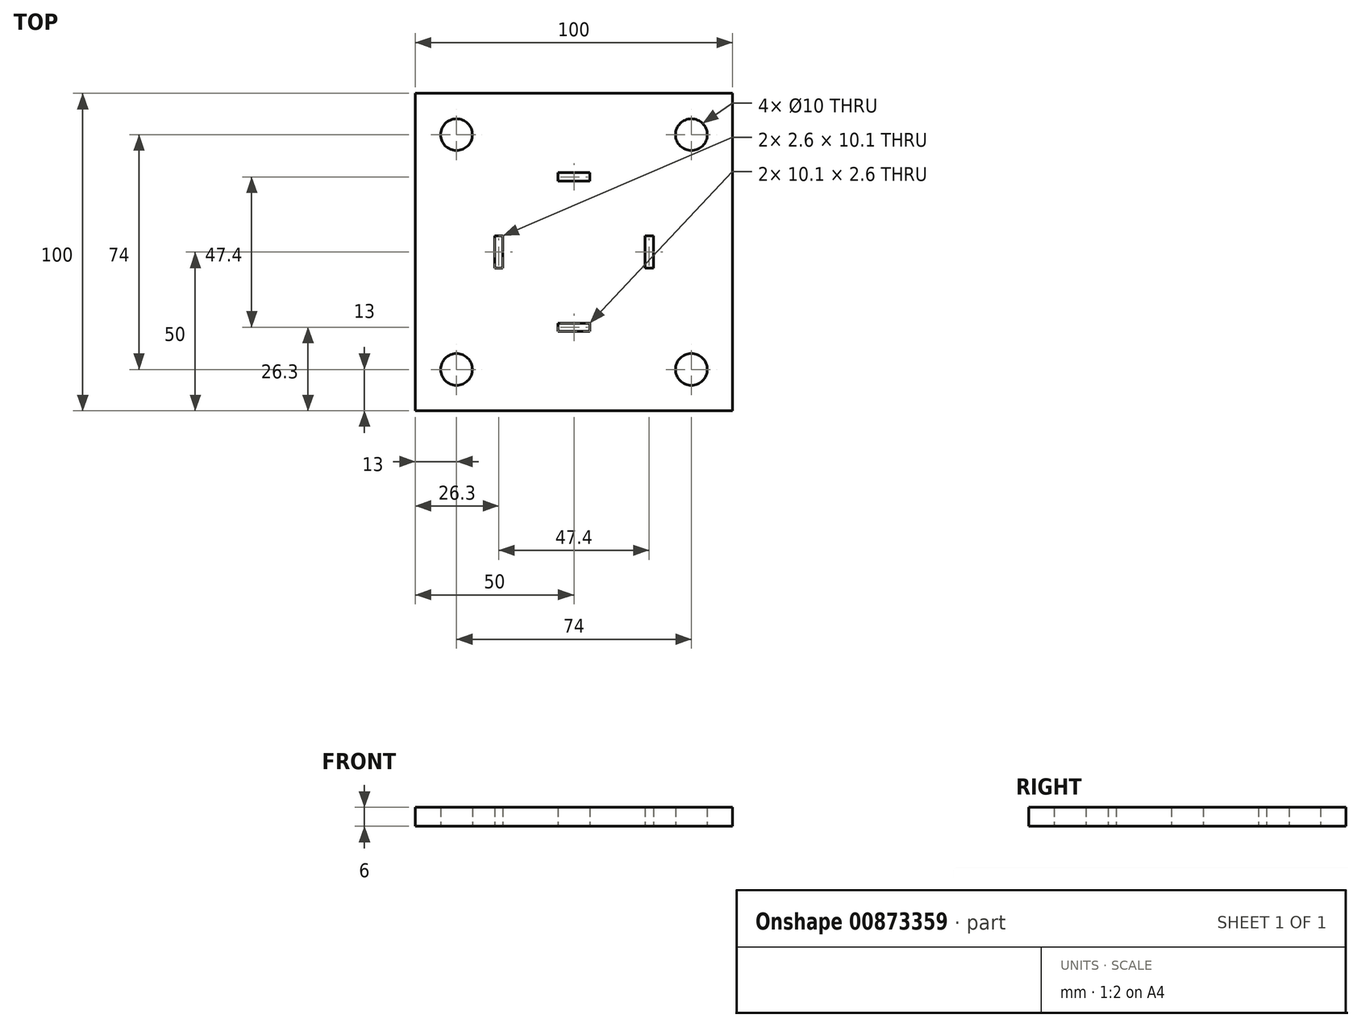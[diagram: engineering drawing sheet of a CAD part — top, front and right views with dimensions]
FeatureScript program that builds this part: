
annotation { "Feature Type Name" : "Feature", "Feature Type Description" : "" }
export const myFeature = defineFeature(function(context is Context, id is Id, definition is map)
    precondition{}
    {
        {
            var Q0;
            Q0=qCreatedBy(makeId("Top.planeOp"),FACE);
            var sketch = newSketch(context, id + "F0", { "sketchPlane" : qUnion([Q0])});
            skLineSegment(sketch, "E0.bottom", {"start": v(-50, 50) * mm, "end": v(50, 50) * mm});
            skLineSegment(sketch, "E0.top", {"start": v(-50, -50) * mm, "end": v(50, -50) * mm});
            skLineSegment(sketch, "E0.left", {"start": v(-50, 50) * mm, "end": v(-50, -50) * mm});
            skLineSegment(sketch, "E0.right", {"start": v(50, 50) * mm, "end": v(50, -50) * mm});
            skPoint(sketch, "E0.middle", {"position": v(0, 0) * mm});
            skLineSegment(sketch, "E1", {"start": v(-50, 50) * mm, "end": v(50, -50) * mm, "construction": true});
            skLineSegment(sketch, "E2", {"start": v(50, 50) * mm, "end": v(-50, -50) * mm, "construction": true});
            skLineSegment(sketch, "E3.bottom", {"start": v(25, 25) * mm, "end": v(-25, 25) * mm, "construction": true});
            skLineSegment(sketch, "E3.top", {"start": v(25, -25) * mm, "end": v(-25, -25) * mm, "construction": true});
            skLineSegment(sketch, "E3.left", {"start": v(25, 25) * mm, "end": v(25, -25) * mm, "construction": true});
            skLineSegment(sketch, "E3.right", {"start": v(-25, 25) * mm, "end": v(-25, -25) * mm, "construction": true});
            skLineSegment(sketch, "E4.bottom", {"start": v(-5.05, 25) * mm, "end": v(5.05, 25) * mm});
            skLineSegment(sketch, "E4.top", {"start": v(-5.05, 22.4) * mm, "end": v(5.05, 22.4) * mm});
            skLineSegment(sketch, "E4.left", {"start": v(-5.05, 25) * mm, "end": v(-5.05, 22.4) * mm});
            skLineSegment(sketch, "E4.right", {"start": v(5.05, 25) * mm, "end": v(5.05, 22.4) * mm});
            skLineSegment(sketch, "E5.bottom", {"start": v(25, 5.05) * mm, "end": v(22.4, 5.05) * mm});
            skLineSegment(sketch, "E5.top", {"start": v(25, -5.05) * mm, "end": v(22.4, -5.05) * mm});
            skLineSegment(sketch, "E5.left", {"start": v(25, 5.05) * mm, "end": v(25, -5.05) * mm});
            skLineSegment(sketch, "E5.right", {"start": v(22.4, 5.05) * mm, "end": v(22.4, -5.05) * mm});
            skLineSegment(sketch, "E6.bottom", {"start": v(5.05, -25) * mm, "end": v(-5.05, -25) * mm});
            skLineSegment(sketch, "E6.top", {"start": v(5.05, -22.4) * mm, "end": v(-5.05, -22.4) * mm});
            skLineSegment(sketch, "E6.left", {"start": v(5.05, -25) * mm, "end": v(5.05, -22.4) * mm});
            skLineSegment(sketch, "E6.right", {"start": v(-5.05, -25) * mm, "end": v(-5.05, -22.4) * mm});
            skLineSegment(sketch, "E7.bottom", {"start": v(-25, 5.05) * mm, "end": v(-22.4, 5.05) * mm});
            skLineSegment(sketch, "E7.top", {"start": v(-25, -5.05) * mm, "end": v(-22.4, -5.05) * mm});
            skLineSegment(sketch, "E7.left", {"start": v(-25, 5.05) * mm, "end": v(-25, -5.05) * mm});
            skLineSegment(sketch, "E7.right", {"start": v(-22.4, 5.05) * mm, "end": v(-22.4, -5.05) * mm});
            skCircle(sketch, "E8", {"center": v(-37, 37) * mm, "radius": 5 * mm});
            skCircle(sketch, "E9", {"center": v(37, 37) * mm, "radius": 5 * mm});
            skCircle(sketch, "E10", {"center": v(-37, -37) * mm, "radius": 5 * mm});
            skCircle(sketch, "E11", {"center": v(37, -37) * mm, "radius": 5 * mm});
            skSolve(sketch);
        }
        {
            var Q0;
            Q0 = qSketchRegion(id + "F0", true);
            extrude(context, id + "F1", {"entities" : qUnion([Q0]), "depth" : 6 * mm, "offsetDistance" : 25 * mm});
        }
    });
